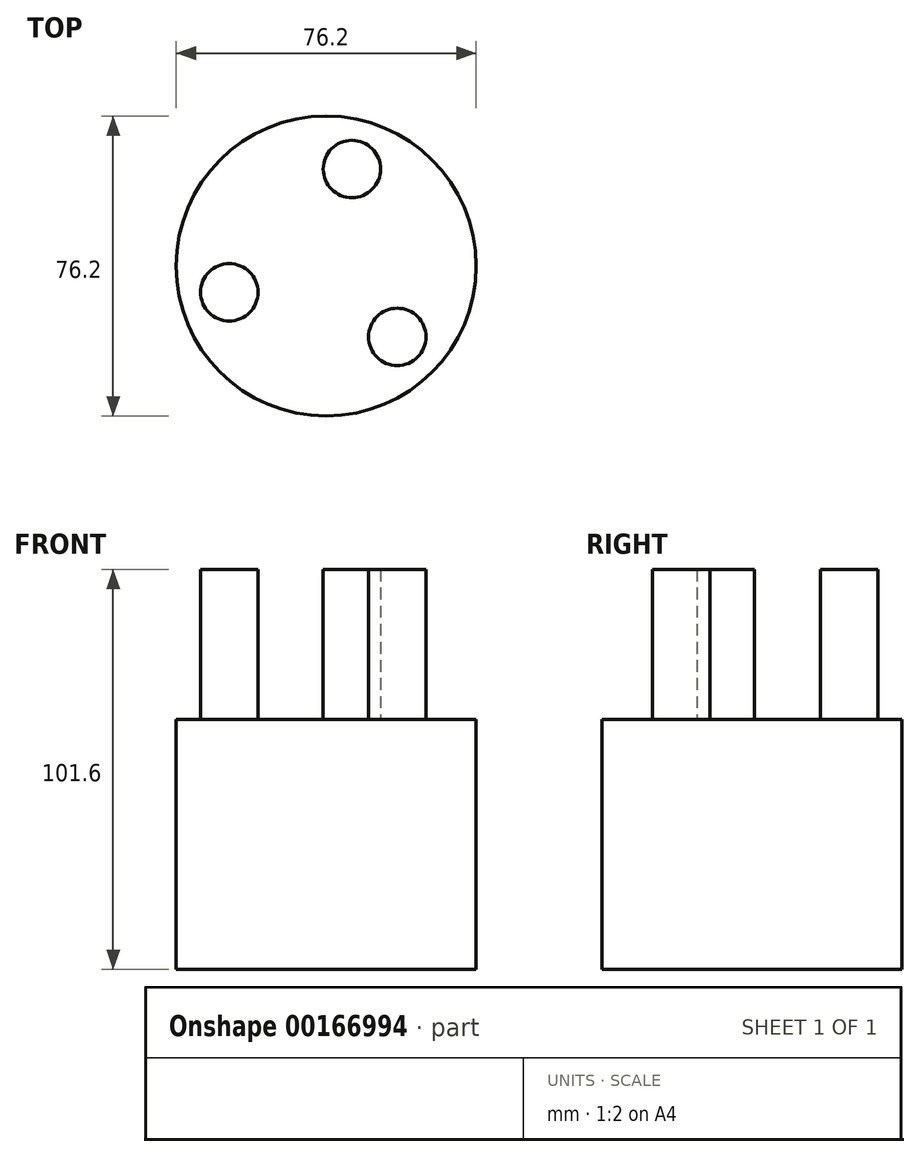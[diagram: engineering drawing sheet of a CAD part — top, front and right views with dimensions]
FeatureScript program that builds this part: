
annotation { "Feature Type Name" : "Feature", "Feature Type Description" : "" }
export const myFeature = defineFeature(function(context is Context, id is Id, definition is map)
    precondition{}
    {
        {
            var Q0;
            Q0=qCreatedBy(makeId("Top.planeOp"),FACE);
            var sketch = newSketch(context, id + "F0", { "sketchPlane" : qUnion([Q0])});
            skCircle(sketch, "E0", {"center": v(0, 0) * mm, "radius": 38.1 * mm});
            skSolve(sketch);
        }
        {
            var Q0;
            Q0 = qSketchRegion(id + "F0", true);
            extrude(context, id + "F1", {"entities" : qUnion([Q0]), "depth" : 63.5 * mm});
        }
        {
            var Q0;
            Q0=qCreatedBy(makeId("Top.planeOp"),FACE);
            var sketch = newSketch(context, id + "F2", { "sketchPlane" : qUnion([Q0])});
            skPoint(sketch, "E1.0.midPoint", {"position": v(12.3, 3.33) * mm});
            skCircle(sketch, "E2", {"center": v(6.54, 24.65) * mm, "radius": 7.3 * mm});
            skCircle(sketch, "E3", {"center": v(-24.62, -6.66) * mm, "radius": 7.3 * mm});
            skCircle(sketch, "E4", {"center": v(18.08, -18) * mm, "radius": 7.3 * mm});
            skSolve(sketch);
        }
        {
            var Q0;
            Q0 = qSketchRegion(id + "F2", true);
            extrude(context, id + "F3", {"entities" : qUnion([Q0]), "operationType" : NewBodyOperationType.ADD, "depth" : 101.6 * mm});
        }
    });
